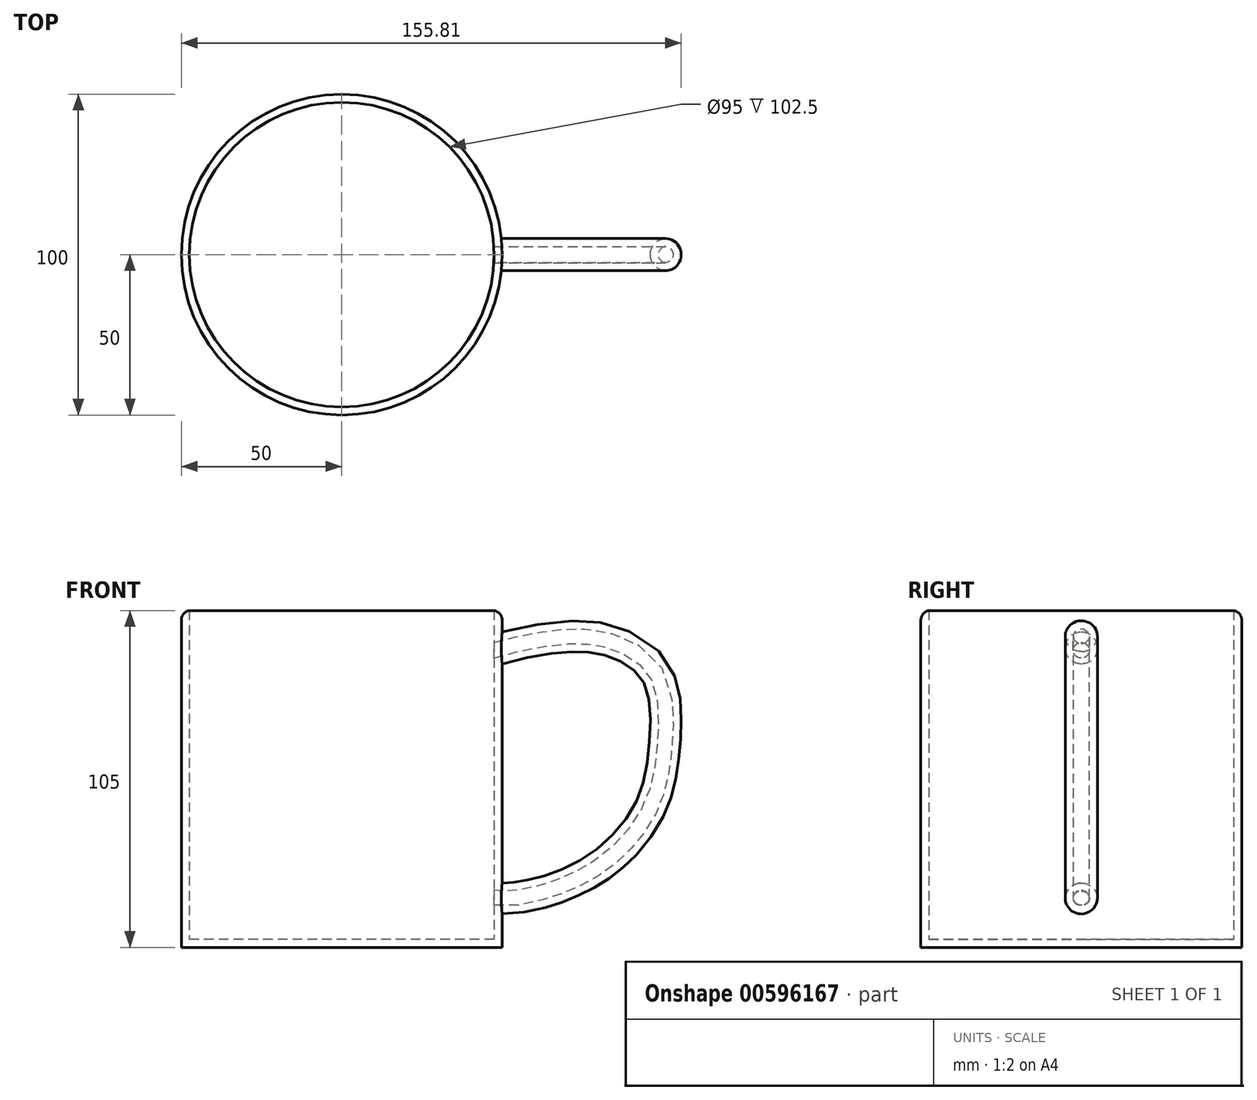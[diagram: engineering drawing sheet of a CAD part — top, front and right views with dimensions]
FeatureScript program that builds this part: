
annotation { "Feature Type Name" : "Feature", "Feature Type Description" : "" }
export const myFeature = defineFeature(function(context is Context, id is Id, definition is map)
    precondition{}
    {
        {
            var Q0;
            Q0=qCreatedBy(makeId("Top.planeOp"),FACE);
            var sketch = newSketch(context, id + "F0", { "sketchPlane" : qUnion([Q0])});
            skCircle(sketch, "E0", {"center": v(0, 0) * mm, "radius": 50 * mm});
            skSolve(sketch);
        }
        {
            var Q0;
            Q0 = qSketchRegion(id + "F0", true);
            extrude(context, id + "F1", {"entities" : qUnion([Q0]), "depth" : 105 * mm, "offsetDistance" : 25 * mm});
        }
        {
            var Q0;
            Q0=qCreatedBy(makeId("Front.planeOp"),FACE);
            var sketch = newSketch(context, id + "F2", { "sketchPlane" : qUnion([Q0])});
            skFitSpline(sketch, "E1", {"points": [v(38.63, 86.25) * mm, v(66.65, 94.5) * mm, v(82.88, 93.6) * mm, v(95.97, 84.8) * mm, v(98.67, 64.96) * mm, v(94.16, 44.2) * mm, v(79.5, 27.3) * mm, v(61.9, 19.17) * mm, v(50.63, 17.37) * mm, v(44.24, 18.23) * mm, v(32.37, 21.09) * mm], "startDerivative": vector(158.21, 105.6) * mm, "endDerivative": vector(-202.93, 62.68) * mm});
            skSolve(sketch);
        }
        {
            var Q0;
            Q0=qCreatedBy(makeId("Right.planeOp"),FACE);
            cPlane(context, id + "F3", {"entities" : qUnion([Q0]), "cplaneType" : CPlaneType.OFFSET, "offset" : 50 * mm, "width" : 150 * mm, "height" : 150 * mm});
        }
        {
            var Q0;
            Q0=qCreatedBy(id+"F3.planeOp",FACE);
            var sketch = newSketch(context, id + "F4", { "sketchPlane" : qUnion([Q0])});
            skCircle(sketch, "E2", {"center": v(0, 93.37) * mm, "radius": 5 * mm});
            skSolve(sketch);
        }
        {
            var Q0;
            Q0=makeQuery(id+"F4.imprint","IMPRINT",FACE,{"disambiguationData":[TD([[makeQuery(id+"F4.imprint","IMPRINT",EDGE,{"derivedFrom":sQuery(id+"F4.wireOp",EDGE,"E2")}),1.0]])]});
            var Q1;
            Q1=sQuery(id+"F2.wireOp",EDGE,"E1");
            sweep(context, id + "F5", {"operationType" : NewBodyOperationType.ADD, "profiles" : qUnion([Q0]), "path" : qUnion([Q1])});
        }
        {
            var Q0;
            Q0=makeQuery(id+"F1.opExtrude","CAP_FACE",FACE,{"disambiguationData":[OSD([sQuery(id+"F0.wireOp",EDGE,"E0")])],"isStart":false});
            shell(context, id + "F6", {"entities" : qUnion([Q0]), "thickness" : 2.5 * mm});
        }
        {
            var Q0;
            Q0=makeQuery(id+"F1.opExtrude","CAP_EDGE",EDGE,{"disambiguationData":[OSD([sQuery(id+"F0.wireOp",EDGE,"E0")])],"isStart":false});
            fillet(context, id + "F7", {"entities" : qUnion([Q0]), "radius" : 3 * mm, "tangentPropagation" : true, "allowEdgeOverflow" : false});
        }
    });
